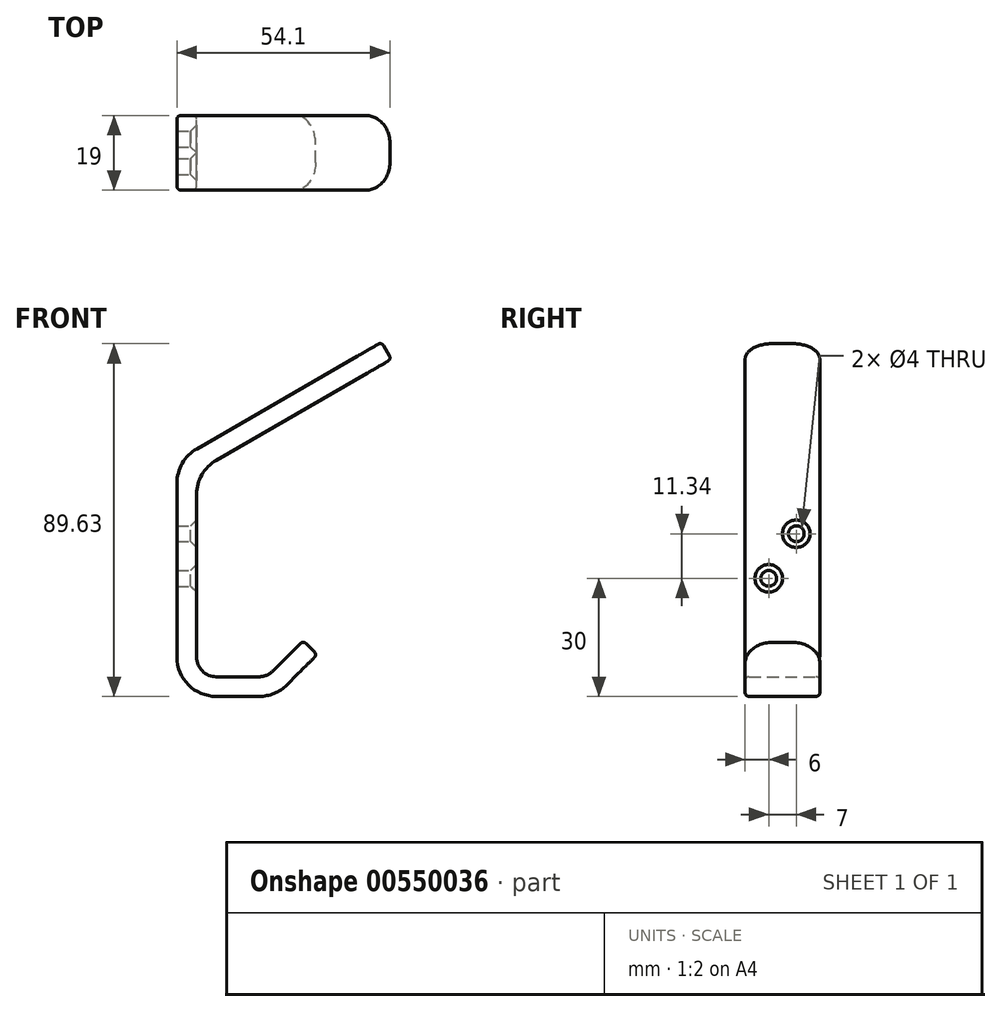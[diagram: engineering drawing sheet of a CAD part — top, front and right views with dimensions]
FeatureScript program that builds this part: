
annotation { "Feature Type Name" : "Feature", "Feature Type Description" : "" }
export const myFeature = defineFeature(function(context is Context, id is Id, definition is map)
    precondition{}
    {
        {
            var Q0;
            Q0=qCreatedBy(makeId("Front.planeOp"),FACE);
            var sketch = newSketch(context, id + "F0", { "sketchPlane" : qUnion([Q0])});
            skLineSegment(sketch, "E0", {"start": v(0, 0) * mm, "end": v(0, 60) * mm});
            skLineSegment(sketch, "E1", {"start": v(0, 0) * mm, "end": v(25, 0) * mm});
            skLineSegment(sketch, "E2", {"start": v(25, 0) * mm, "end": v(35.6, 10.6) * mm});
            skLineSegment(sketch, "E3", {"start": v(35.6, 10.6) * mm, "end": v(32.07, 14.14) * mm});
            skLineSegment(sketch, "E4", {"start": v(32.07, 14.14) * mm, "end": v(22.93, 5) * mm});
            skLineSegment(sketch, "E5", {"start": v(0, 60) * mm, "end": v(51.96, 90) * mm});
            skLineSegment(sketch, "E6", {"start": v(51.96, 90) * mm, "end": v(54.46, 85.67) * mm});
            skLineSegment(sketch, "E7", {"start": v(54.46, 85.67) * mm, "end": v(5, 57.11) * mm});
            skLineSegment(sketch, "E8", {"start": v(4.23, 5) * mm, "end": v(22.93, 5) * mm});
            skLineSegment(sketch, "E9", {"start": v(5, 5) * mm, "end": v(5, 57.11) * mm});
            skPoint(sketch, "E10.orphan", {"position": v(4.23, 56.67) * mm});
            skSolve(sketch);
        }
        {
            var Q0;
            Q0 = qSketchRegion(id + "F0", true);
            extrude(context, id + "F1", {"entities" : qUnion([Q0]), "depth" : 19 * mm, "offsetDistance" : 25 * mm});
        }
        {
            var Q0;
            Q0=makeQuery(id+"F1.opExtrude","SWEPT_EDGE",EDGE,{"disambiguationData":[OSD([sQuery(id+"F0.wireOp",EDGE,"E7"),sQuery(id+"F0.wireOp",EDGE,"E9")])]});
            fillet(context, id + "F2", {"entities" : qUnion([Q0]), "radius" : 10 * mm, "tangentPropagation" : true, "allowEdgeOverflow" : false});
        }
        {
            var Q0;
            Q0=makeQuery(id+"F1.opExtrude","SWEPT_EDGE",EDGE,{"disambiguationData":[OSD([sQuery(id+"F0.wireOp",EDGE,"E8"),sQuery(id+"F0.wireOp",EDGE,"E9")])]});
            fillet(context, id + "F3", {"entities" : qUnion([Q0]), "radius" : 5 * mm, "tangentPropagation" : true, "allowEdgeOverflow" : false});
        }
        {
            var Q0;
            Q0=makeQuery(id+"F1.opExtrude","SWEPT_EDGE",EDGE,{"disambiguationData":[OSD([sQuery(id+"F0.wireOp",EDGE,"E0"),sQuery(id+"F0.wireOp",EDGE,"E1")])]});
            fillet(context, id + "F4", {"entities" : qUnion([Q0]), "radius" : 10 * mm, "tangentPropagation" : true, "allowEdgeOverflow" : false});
        }
        {
            var Q0;
            Q0=makeQuery(id+"F1.opExtrude","SWEPT_EDGE",EDGE,{"disambiguationData":[OSD([sQuery(id+"F0.wireOp",EDGE,"E0"),sQuery(id+"F0.wireOp",EDGE,"E5")])]});
            fillet(context, id + "F5", {"entities" : qUnion([Q0]), "radius" : 10.1 * mm, "tangentPropagation" : true, "allowEdgeOverflow" : false});
        }
        {
            var Q0;
            Q0=makeQuery(id+"F1.opExtrude","SWEPT_EDGE",EDGE,{"disambiguationData":[OSD([sQuery(id+"F0.wireOp",EDGE,"E4"),sQuery(id+"F0.wireOp",EDGE,"E8")])]});
            fillet(context, id + "F6", {"entities" : qUnion([Q0]), "radius" : 5 * mm, "tangentPropagation" : true, "allowEdgeOverflow" : false});
        }
        {
            var Q0;
            Q0=makeQuery(id+"F1.opExtrude","SWEPT_EDGE",EDGE,{"disambiguationData":[OSD([sQuery(id+"F0.wireOp",EDGE,"E1"),sQuery(id+"F0.wireOp",EDGE,"E2")])]});
            fillet(context, id + "F7", {"entities" : qUnion([Q0]), "radius" : 10 * mm, "tangentPropagation" : true, "allowEdgeOverflow" : false});
        }
        {
            var Q0;
            Q0=makeQuery(id+"F1.opExtrude","CAP_EDGE",EDGE,{"disambiguationData":[OSD([sQuery(id+"F0.wireOp",EDGE,"E6")])],"isStart":false});
            var Q1;
            Q1=makeQuery(id+"F1.opExtrude","CAP_EDGE",EDGE,{"disambiguationData":[OSD([sQuery(id+"F0.wireOp",EDGE,"E6")])],"isStart":true});
            fillet(context, id + "F8", {"entities" : qUnion([Q0, Q1]), "radius" : 7 * mm, "tangentPropagation" : true, "allowEdgeOverflow" : false});
        }
        {
            var Q0;
            Q0=makeQuery(id+"F1.opExtrude","CAP_EDGE",EDGE,{"disambiguationData":[OSD([sQuery(id+"F0.wireOp",EDGE,"E3")])],"isStart":false});
            fillet(context, id + "F9", {"entities" : qUnion([Q0]), "radius" : 7 * mm, "tangentPropagation" : true, "allowEdgeOverflow" : false});
        }
        {
            var Q0;
            Q0=makeQuery(id+"F1.opExtrude","CAP_EDGE",EDGE,{"disambiguationData":[OSD([sQuery(id+"F0.wireOp",EDGE,"E3")])],"isStart":true});
            fillet(context, id + "F10", {"entities" : qUnion([Q0]), "radius" : 7 * mm, "tangentPropagation" : true, "allowEdgeOverflow" : false});
        }
        {
            var Q0;
            Q0=makeQuery(id+"F1.opExtrude","SWEPT_FACE",FACE,{"disambiguationData":[OSD([sQuery(id+"F0.wireOp",EDGE,"E5")])]});
            fillet(context, id + "F11", {"entities" : qUnion([Q0]), "radius" : 1 * mm, "tangentPropagation" : true, "allowEdgeOverflow" : false});
        }
        {
            var Q0;
            Q0=makeQuery(id+"F1.opExtrude","SWEPT_FACE",FACE,{"disambiguationData":[OSD([sQuery(id+"F0.wireOp",EDGE,"E4")])]});
            fillet(context, id + "F12", {"entities" : qUnion([Q0]), "radius" : 1 * mm, "tangentPropagation" : true, "allowEdgeOverflow" : false});
        }
        {
            var Q0;
            Q0=makeQuery(id+"F1.opExtrude","SWEPT_FACE",FACE,{"disambiguationData":[OSD([sQuery(id+"F0.wireOp",EDGE,"E9")])]});
            var sketch = newSketch(context, id + "F13", { "sketchPlane" : qUnion([Q0])});
            skPoint(sketch, "E11", {"position": v(-6, 41.34) * mm});
            skPoint(sketch, "E12", {"position": v(-13, 30) * mm});
            skSolve(sketch);
        }
        {
            var Q0;
            Q0=sQuery(id+"F13.wireOp",VERTEX,"E11");
            var Q1;
            Q1=sQuery(id+"F13.wireOp",VERTEX,"E12");
            var Q2;
            Q2=makeQuery(id+"F1.opExtrude","SWEPT_BODY",BODY,{"disambiguationData":[OSD([sQuery(id+"F0.wireOp",EDGE,"E0"),sQuery(id+"F0.wireOp",EDGE,"E1"),sQuery(id+"F0.wireOp",EDGE,"E2"),sQuery(id+"F0.wireOp",EDGE,"E3"),sQuery(id+"F0.wireOp",EDGE,"E4"),sQuery(id+"F0.wireOp",EDGE,"E5"),sQuery(id+"F0.wireOp",EDGE,"E6"),sQuery(id+"F0.wireOp",EDGE,"E7"),sQuery(id+"F0.wireOp",EDGE,"E8"),sQuery(id+"F0.wireOp",EDGE,"E9")])]});
            hole(context, id + "F14", {"style" : HoleStyle.C_SINK, "endStyle" : HoleEndStyle.THROUGH, "holeDiameter" : 4 * mm, "cSinkDiameter" : 7 * mm, "cSinkAngle" : 90 * degree, "majorDiameter" : 5 * mm, "isTappedThrough" : true, "tappedDepth" : 12 * mm, "tapClearance" : 3, "locations" : qUnion([Q0, Q1]), "scope" : qUnion([Q2])});
        }
    });
